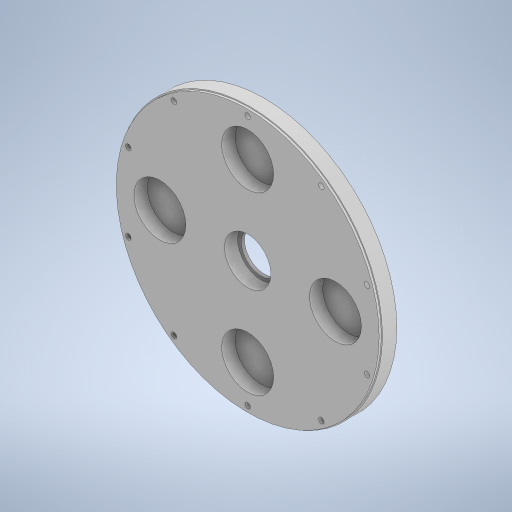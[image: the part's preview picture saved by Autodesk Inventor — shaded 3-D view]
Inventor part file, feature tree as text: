
AUTODESK INVENTOR PART (.ipt)
format: ipt  version: 2024.2 (Build 282272000, 272)  size: 327,168 bytes
history: native  units: mm
features: extrude x6, sketch x6
ambient origin geometry x8: Origin, YZ Plane, XZ Plane, XY Plane, X Axis, Y Axis, Z Axis, Center Point
bodies: Solid1 (feature_tree)
feature tree (12):
  extrude  "Extrusion1"  Depth=36.0mm
  extrude  "Extrusion2"  Depth=15.0mm
  extrude  "Extrusion3"  Depth=47.0mm
  extrude  "Extrusion4"  Depth=12.0mm TaperAngle=0.0deg
  extrude  "Extrusion5"  Depth=12.0mm TaperAngle=0.0deg
  extrude  "Extrusion6"  Depth=2.0mm
  sketch  "Sketch1"  dims[d0=240.0mm d1=36.0mm]
  sketch  "Sketch2"  dims[d2=15.0mm d3=0.0mm d5=47.0mm]
  sketch  "Sketch3"  dims[d7=47.0mm d8=47.0mm]
  sketch  "Sketch4"  dims[d9=47.0mm d10=12.0mm d11=0.0mm]
  sketch  "Sketch5"  dims[d12=42.0mm d13=12.0mm d14=0.0mm]
  sketch  "Sketch7"  dims[d15=238.0mm d16=240.0mm d17=2.0mm d18=0.0mm d19=113.556mm d20=5.0mm d22=100.0mm d24=360.0deg d26=15.0mm d27=0.0mm d28=12.24mm d29=100.0mm d31=360.0deg d33=2.0mm d34=0.0mm d35=0.5mm d36=0.872665mm]
